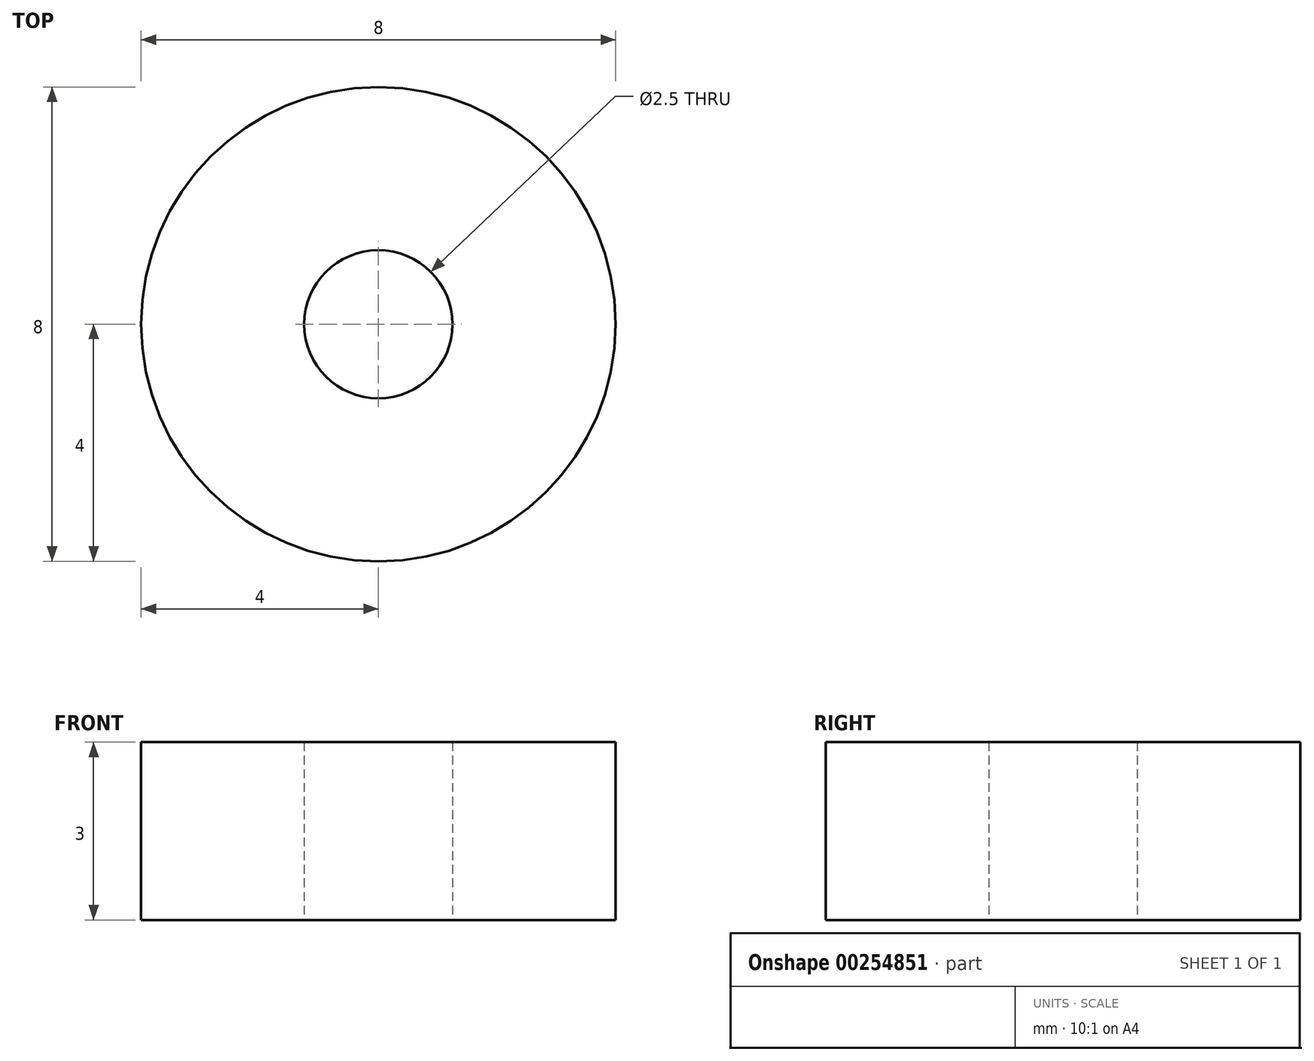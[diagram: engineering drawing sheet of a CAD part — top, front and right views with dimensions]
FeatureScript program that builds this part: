
annotation { "Feature Type Name" : "Feature", "Feature Type Description" : "" }
export const myFeature = defineFeature(function(context is Context, id is Id, definition is map)
    precondition{}
    {
        {
            var Q0;
            Q0=qCreatedBy(makeId("Top.planeOp"),FACE);
            var sketch = newSketch(context, id + "F0", { "sketchPlane" : qUnion([Q0])});
            skCircle(sketch, "E0", {"center": v(0, 0) * mm, "radius": 1.25 * mm});
            skCircle(sketch, "E1", {"center": v(0, 0) * mm, "radius": 4 * mm});
            skSolve(sketch);
        }
        {
            var Q0;
            Q0 = qSketchRegion(id + "F0", true);
            extrude(context, id + "F1", {"entities" : qUnion([Q0]), "depth" : 3 * mm});
        }
    });
